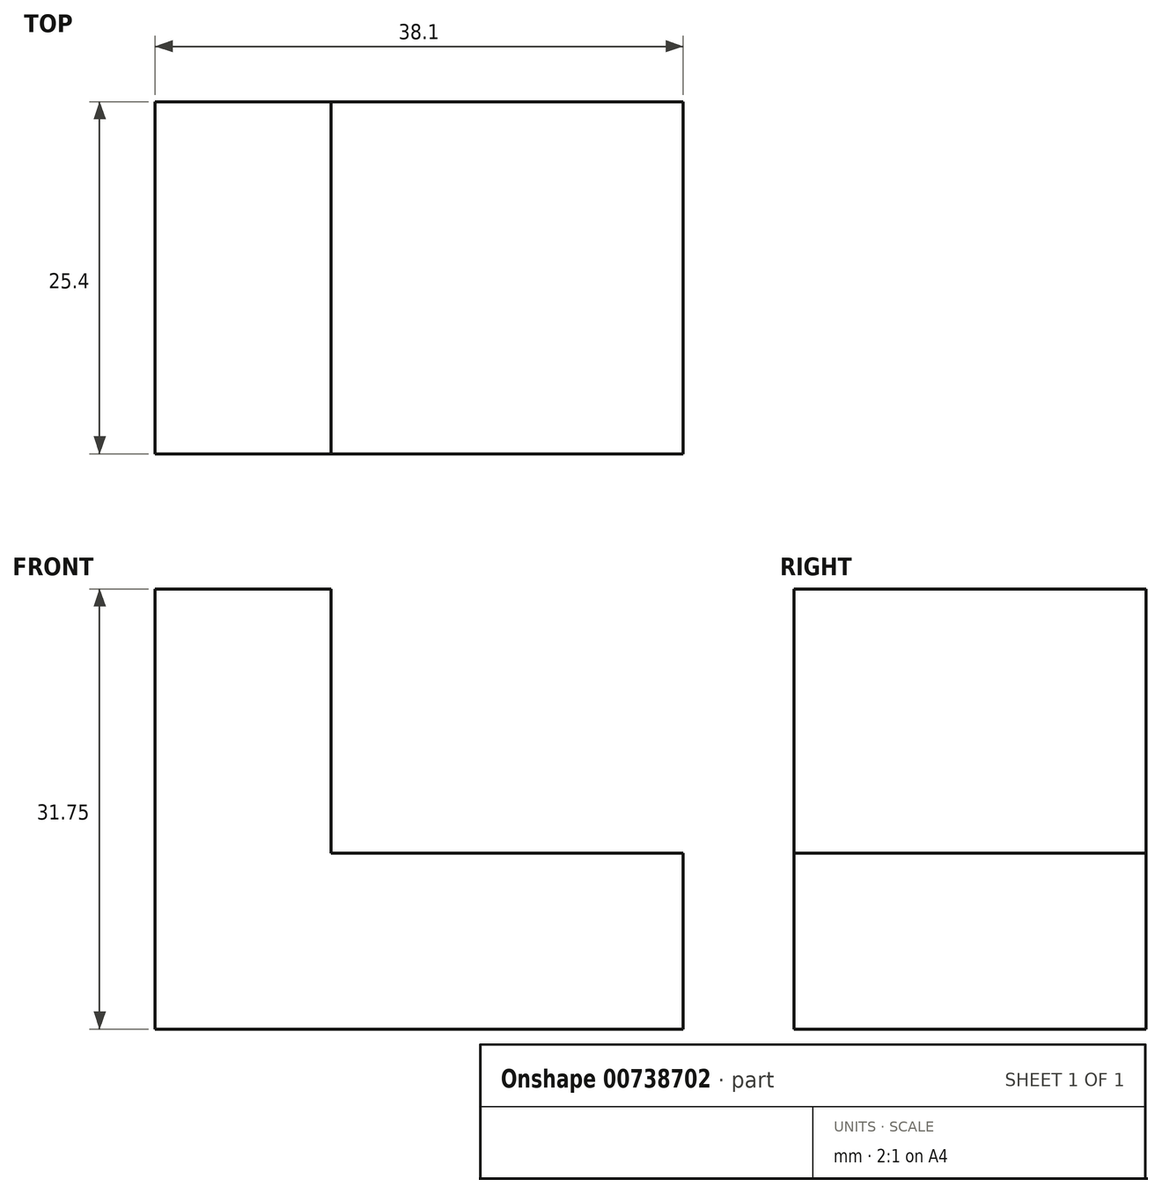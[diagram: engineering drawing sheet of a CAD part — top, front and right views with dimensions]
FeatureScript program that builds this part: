
annotation { "Feature Type Name" : "Feature", "Feature Type Description" : "" }
export const myFeature = defineFeature(function(context is Context, id is Id, definition is map)
    precondition{}
    {
        {
            var Q0;
            Q0=qCreatedBy(makeId("Front.planeOp"),FACE);
            var sketch = newSketch(context, id + "F0", { "sketchPlane" : qUnion([Q0])});
            skLineSegment(sketch, "E0", {"start": v(0, 31.75) * mm, "end": v(0, 0) * mm});
            skLineSegment(sketch, "E1", {"start": v(0, 0) * mm, "end": v(38.1, 0) * mm});
            skLineSegment(sketch, "E2", {"start": v(38.1, 0) * mm, "end": v(38.1, 12.7) * mm});
            skLineSegment(sketch, "E3", {"start": v(38.1, 12.7) * mm, "end": v(12.7, 12.7) * mm});
            skLineSegment(sketch, "E4", {"start": v(12.7, 12.7) * mm, "end": v(12.7, 31.75) * mm});
            skLineSegment(sketch, "E5", {"start": v(12.7, 31.75) * mm, "end": v(0, 31.75) * mm});
            skSolve(sketch);
        }
        {
            var Q0;
            Q0 = qSketchRegion(id + "F0", true);
            var Q1;
            Q1=makeQuery(id+"F0.imprint","IMPRINT",FACE,{"disambiguationData":[TD([[makeQuery(id+"F0.imprint","IMPRINT",EDGE,{"derivedFrom":sQuery(id+"F0.wireOp",EDGE,"E0")}),1.0]])]});
            extrude(context, id + "F1", {"entities" : qUnion([Q0, Q1]), "depth" : 25.4 * mm, "offsetDistance" : 25.4 * mm});
        }
    });
